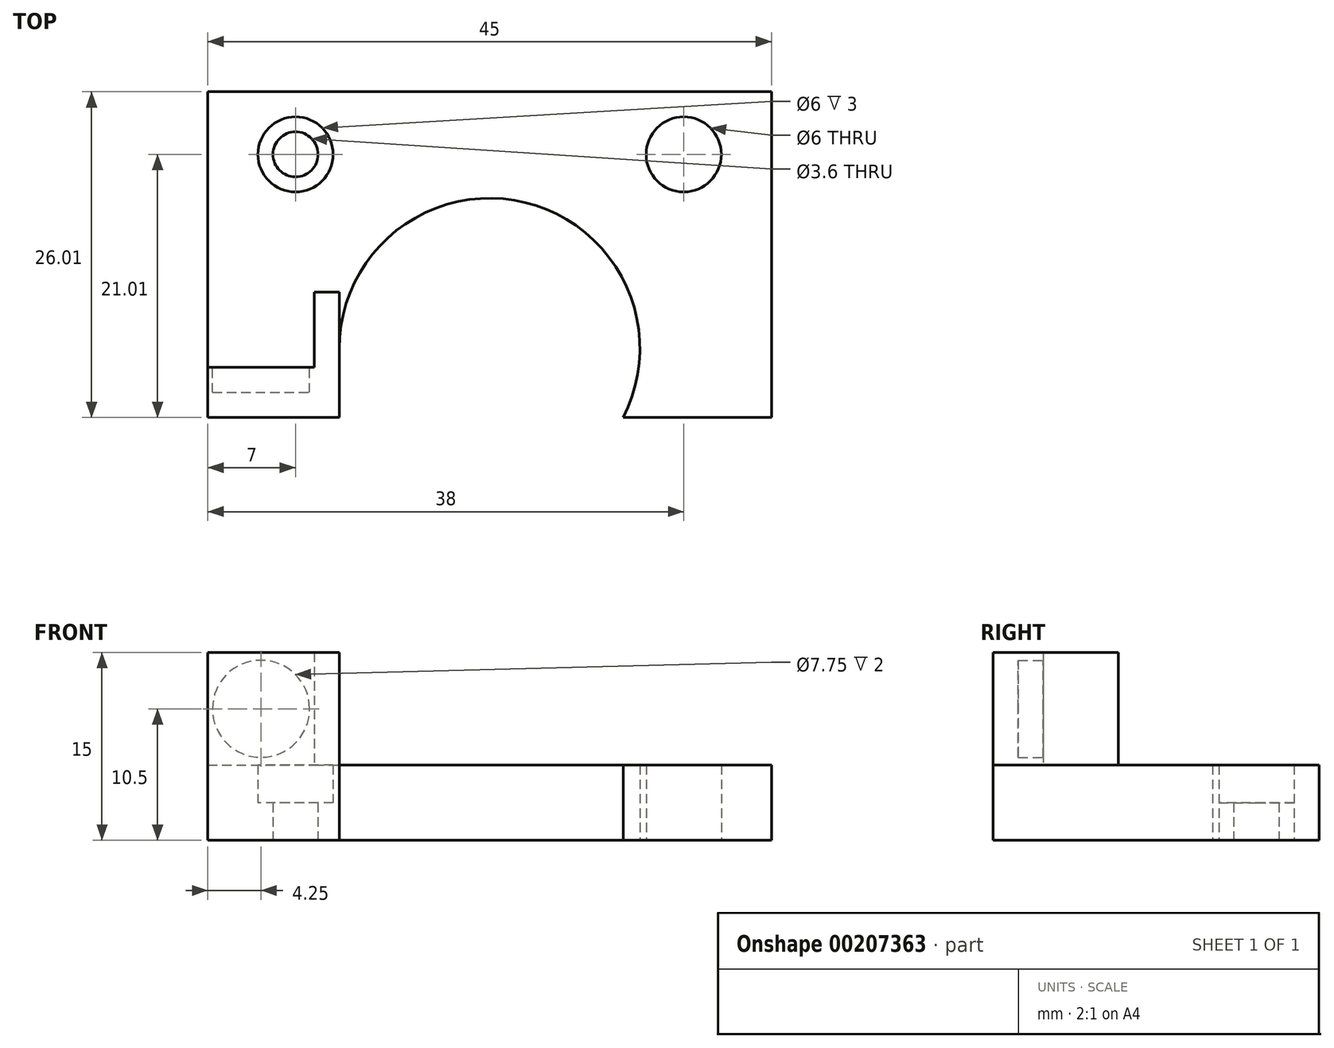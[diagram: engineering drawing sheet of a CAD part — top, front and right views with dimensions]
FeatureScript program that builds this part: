
annotation { "Feature Type Name" : "Feature", "Feature Type Description" : "" }
export const myFeature = defineFeature(function(context is Context, id is Id, definition is map)
    precondition{}
    {
        {
            var Q0;
            Q0=qCreatedBy(makeId("Top.planeOp"),FACE);
            var sketch = newSketch(context, id + "F0", { "sketchPlane" : qUnion([Q0])});
            skLineSegment(sketch, "E0", {"start": v(22.5, -5.5) * mm, "end": v(22.5, 20.5) * mm});
            skCircle(sketch, "E1", {"center": v(-15.5, 15.5) * mm, "radius": 1.8 * mm});
            skCircle(sketch, "E2", {"center": v(-15.5, 15.5) * mm, "radius": 3 * mm});
            skCircle(sketch, "E3", {"center": v(0, 0) * mm, "radius": 12 * mm});
            skLineSegment(sketch, "E4", {"start": v(-22.5, 20.5) * mm, "end": v(22.5, 20.5) * mm});
            skCircle(sketch, "E5.MirrorC", {"center": v(15.5, 15.5) * mm, "radius": 3 * mm});
            skCircle(sketch, "E6.MirrorC", {"center": v(15.5, 15.5) * mm, "radius": 1.8 * mm});
            skLineSegment(sketch, "E7", {"start": v(-22.5, -5.5) * mm, "end": v(-22.5, 20.5) * mm});
            skLineSegment(sketch, "E8", {"start": v(-22.5, -5.5) * mm, "end": v(-12, -5.5) * mm});
            skLineSegment(sketch, "E9", {"start": v(-12, -5.5) * mm, "end": v(-12, 4.5) * mm});
            skLineSegment(sketch, "E10", {"start": v(-12, 4.5) * mm, "end": v(-14, 4.5) * mm});
            skLineSegment(sketch, "E11", {"start": v(-14, 4.5) * mm, "end": v(-14, -1.5) * mm});
            skLineSegment(sketch, "E12", {"start": v(-14, -1.5) * mm, "end": v(-22.5, -1.5) * mm});
            skPoint(sketch, "E13", {"position": v(0, 20.5) * mm});
            skLineSegment(sketch, "E14", {"start": v(-12, -5.5) * mm, "end": v(22.5, -5.5) * mm});
            skSolve(sketch);
        }
        {
            var Q0;
            {var subQ2=sQuery(id+"F0.wireOp",EDGE,"E0");Q0=makeQuery(id+"F0.imprint","IMPRINT",FACE,{"disambiguationData":[TD([[makeQuery(id+"F0.imprint","IMPRINT",EDGE,{"derivedFrom":subQ2}),1.0]])]});}
            var Q1;
            {var subQ0=sQuery(id+"F0.wireOp",EDGE,"E8");Q1=makeQuery(id+"F0.imprint","IMPRINT",FACE,{"disambiguationData":[TD([[makeQuery(id+"F0.imprint","IMPRINT",EDGE,{"derivedFrom":subQ0}),-1.0]])]});}
            var Q2;
            {var subQ3=sQuery(id+"F0.wireOp",EDGE,"E8");Q2=makeQuery(id+"F0.imprint","IMPRINT",FACE,{"disambiguationData":[TD([[makeQuery(id+"F0.imprint","IMPRINT",EDGE,{"derivedFrom":subQ3}),1.0]])]});}
            var Q3;
            Q3=makeQuery(id+"F0.imprint","IMPRINT",FACE,{"disambiguationData":[TD([[makeQuery(id+"F0.imprint","IMPRINT",EDGE,{"derivedFrom":sQuery(id+"F0.wireOp",EDGE,"E5.MirrorC")}),-1.0]])]});
            extrude(context, id + "F1", {"entities" : qUnion([Q0, Q1, Q2, Q3]), "depth" : 6 * mm, "offsetDistance" : 25 * mm});
        }
        {
            var Q0;
            {var subQ0=sQuery(id+"F0.wireOp",EDGE,"E8");Q0=makeQuery(id+"F0.imprint","IMPRINT",FACE,{"disambiguationData":[TD([[makeQuery(id+"F0.imprint","IMPRINT",EDGE,{"derivedFrom":subQ0}),1.0]])]});}
            var Q1;
            {var subQ0=sQuery(id+"F0.wireOp",EDGE,"E14");var subQ1=sQuery(id+"F0.wireOp",EDGE,"E3");var subQ2=makeQuery(id+"F0.imprint","INTERSECT",VERTEX,{"disambiguationData":[OD(0.0)],"derivedFrom":[subQ1,subQ0]});Q1=makeQuery(id+"F0.imprint","IMPRINT",FACE,{"disambiguationData":[TD([[makeQuery(id+"F0.imprint","IMPRINT",EDGE,{"disambiguationData":[TD([[subQ2,1.0]])],"derivedFrom":subQ1}),-1.0]])]});}
            extrude(context, id + "F2", {"entities" : qUnion([Q0, Q1]), "operationType" : NewBodyOperationType.ADD, "offsetDistance" : 25 * mm, "depth" : 15 * mm});
        }
        {
            var Q0;
            Q0=makeQuery(id+"F0.imprint","IMPRINT",FACE,{"disambiguationData":[TD([[makeQuery(id+"F0.imprint","IMPRINT",EDGE,{"derivedFrom":sQuery(id+"F0.wireOp",EDGE,"E1")}),-1.0]])]});
            extrude(context, id + "F3", {"entities" : qUnion([Q0]), "operationType" : NewBodyOperationType.ADD, "depth" : 3 * mm, "offsetDistance" : 25 * mm});
        }
        {
            var Q0;
            Q0=makeQuery(id+"F2.opExtrude","SWEPT_FACE",FACE,{"disambiguationData":[OSD([sQuery(id+"F0.wireOp",EDGE,"E12")])]});
            var sketch = newSketch(context, id + "F4", { "sketchPlane" : qUnion([Q0])});
            skPoint(sketch, "E15", {"position": v(22.5, 10.5) * mm});
            skPoint(sketch, "E16", {"position": v(18.25, 15) * mm});
            skCircle(sketch, "E17", {"center": v(18.25, 10.5) * mm, "radius": 3.88 * mm});
            skSolve(sketch);
        }
        {
            var Q0;
            Q0=makeQuery(id+"F4.imprint","IMPRINT",FACE,{"disambiguationData":[TD([[makeQuery(id+"F4.imprint","IMPRINT",EDGE,{"derivedFrom":sQuery(id+"F4.wireOp",EDGE,"E17")}),1.0]])]});
            extrude(context, id + "F5", {"entities" : qUnion([Q0]), "operationType" : NewBodyOperationType.REMOVE, "oppositeDirection" : true, "depth" : 2 * mm, "offsetDistance" : 25 * mm});
        }
    });
